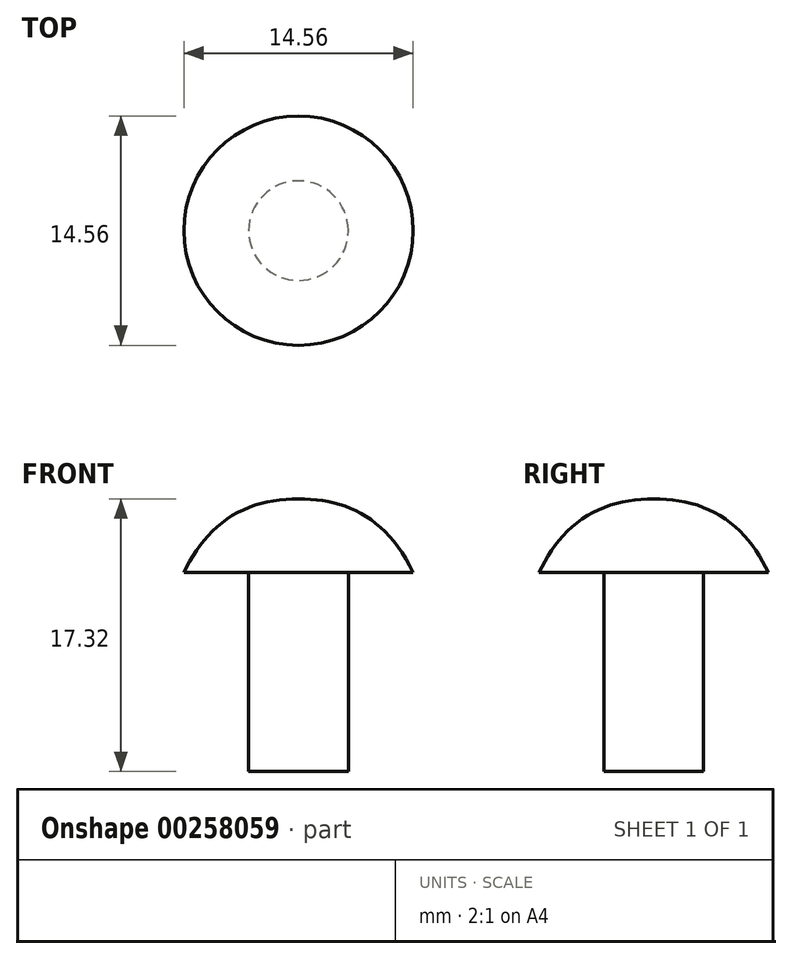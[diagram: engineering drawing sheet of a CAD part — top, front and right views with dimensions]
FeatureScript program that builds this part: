
annotation { "Feature Type Name" : "Feature", "Feature Type Description" : "" }
export const myFeature = defineFeature(function(context is Context, id is Id, definition is map)
    precondition{}
    {
        {
            var Q0;
            Q0=qCreatedBy(makeId("Front.planeOp"),FACE);
            var sketch = newSketch(context, id + "F0", { "sketchPlane" : qUnion([Q0])});
            skLineSegment(sketch, "E0", {"start": v(0, 19.83) * mm, "end": v(0, -16.11) * mm, "construction": true});
            skLineSegment(sketch, "E1.bottom", {"start": v(-3.18, 4.97) * mm, "end": v(3.18, 4.97) * mm});
            skLineSegment(sketch, "E1.top", {"start": v(-3.18, -7.73) * mm, "end": v(3.18, -7.73) * mm});
            skLineSegment(sketch, "E1.left", {"start": v(-3.18, 4.97) * mm, "end": v(-3.18, -7.73) * mm});
            skLineSegment(sketch, "E1.right", {"start": v(3.18, 4.97) * mm, "end": v(3.17, -7.73) * mm});
            skLineSegment(sketch, "E2", {"start": v(0, 4.97) * mm, "end": v(0, 9.66) * mm});
            skLineSegment(sketch, "E3", {"start": v(0, 4.97) * mm, "end": v(7.28, 4.97) * mm});
            skFitSpline(sketch, "E4", {"points": [v(0, 9.66) * mm, v(7.28, 4.97) * mm], "startDerivative": vector(8.93, 0) * mm, "endDerivative": vector(5.1, -10.65) * mm});
            skSolve(sketch);
        }
        {
            var Q0;
            {var subQ0=sQuery(id+"F0.wireOp",EDGE,"E2");Q0=makeQuery(id+"F0.imprint","IMPRINT",FACE,{"disambiguationData":[TD([[makeQuery(id+"F0.imprint","IMPRINT",EDGE,{"derivedFrom":subQ0}),-1.0]])]});}
            var Q1;
            Q1=sQuery(id+"F0.wireOp",EDGE,"E0");
            revolve(context, id + "F1", {"entities" : qUnion([Q0]), "axis" : qUnion([Q1]), "revolveType" : RevolveType.FULL});
        }
        {
            var Q0;
            Q0=qCreatedBy(makeId("Front.planeOp"),FACE);
            var sketch = newSketch(context, id + "F2", { "sketchPlane" : qUnion([Q0])});
            skLineSegment(sketch, "E5.bottom", {"start": v(3.16, -7.66) * mm, "end": v(0, -7.66) * mm});
            skLineSegment(sketch, "E5.top", {"start": v(3.16, 4.97) * mm, "end": v(0, 4.97) * mm});
            skLineSegment(sketch, "E5.left", {"start": v(3.16, -7.66) * mm, "end": v(3.16, 4.97) * mm});
            skLineSegment(sketch, "E5.right", {"start": v(0, -7.66) * mm, "end": v(0, 4.97) * mm});
            skSolve(sketch);
        }
        {
            var Q0;
            Q0 = qSketchRegion(id + "F2", true);
            var Q1;
            Q1=sQuery(id+"F2.wireOp",EDGE,"E5.right");
            revolve(context, id + "F3", {"entities" : qUnion([Q0]), "axis" : qUnion([Q1]), "revolveType" : RevolveType.FULL});
        }
    });
